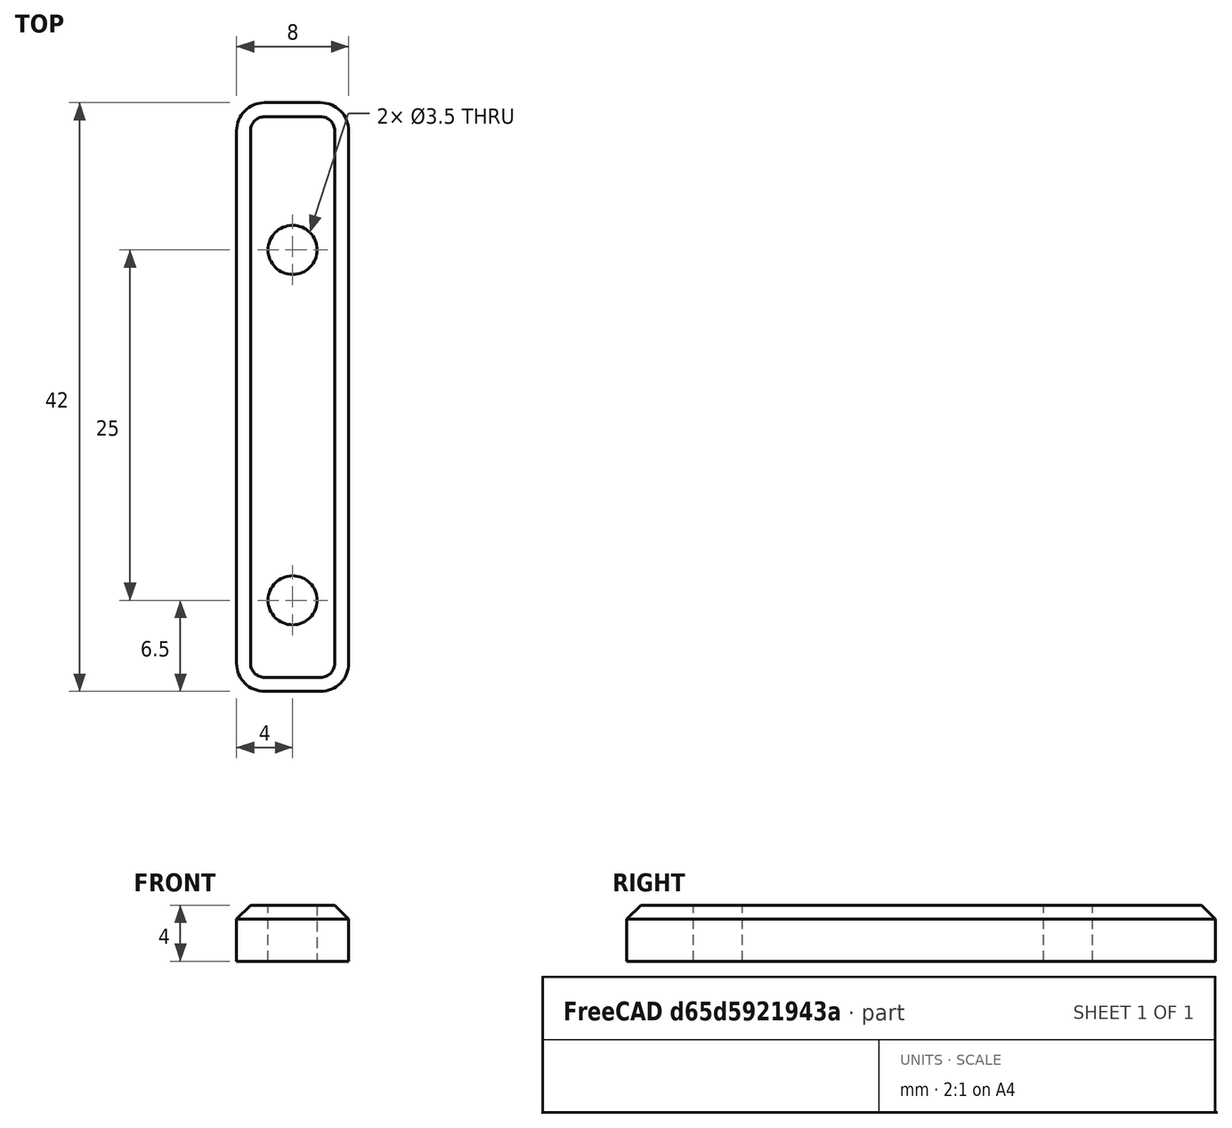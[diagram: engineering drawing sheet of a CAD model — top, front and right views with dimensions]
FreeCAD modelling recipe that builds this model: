
FCSTD DOCUMENT  (FreeCAD 0.19R)
Label: HeadClamp2
License: All rights reserved
LicenseURL: http://en.wikipedia.org/wiki/All_rights_reserved
objects: Sketcher::SketchObject×2, PartDesign::Pad×1, PartDesign::Pocket×1, PartDesign::Fillet×1, PartDesign::Chamfer×1, PartDesign::Body×1, Mesh::Feature×1
note: 11 computed .brp shape members not serialized (recipe doc carries the construction recipe); baked Part::Feature solids carry a one-line shape summary decoded from their .brp

FEATURE [Sketcher::SketchObject] Sketch
  FullyConstrained = true
  MapMode = 5
  Support = -> [XY_Plane]
  sketch-geometry (4):
    g0: LineSegment StartX=-4 StartY=50 StartZ=0 EndX=4 EndY=50 EndZ=0
    g1: LineSegment StartX=4 StartY=50 StartZ=0 EndX=4 EndY=8 EndZ=0
    g2: LineSegment StartX=4 StartY=8 StartZ=0 EndX=-4 EndY=8 EndZ=0
    g3: LineSegment StartX=-4 StartY=8 StartZ=0 EndX=-4 EndY=50 EndZ=0
  constraints (11):
    c: Coincident(g0,g1)
    c: Coincident(g1,g2)
    c: Coincident(g2,g3)
    c: Coincident(g3,g0)
    c: Horizontal(g2)
    c: Vertical(g1)
    c: Vertical(g3)
    c: Distance(g0) = 8
    c: Symmetric(g0,g0,g-2)
    c: DistanceY(g0) = 50
    c: DistanceY(g1) = 8
FEATURE [PartDesign::Pad] Pad
  Direction = (1,1,1)
  Length = 4
  Length2 = 100
  Profile = -> Sketch
  Type = 0
FEATURE [Sketcher::SketchObject] Sketch001
  FullyConstrained = true
  MapMode = 5
  Placement = pos=(0,0,4) rot=(0,0,1;0rad)
  Support = -> [Pad]
  sketch-geometry (2):
    g0: Circle CenterX=0 CenterY=14.5 CenterZ=0 NormalX=0 NormalY=0 NormalZ=1 AngleXU=0 Radius=1.75
    g1: Circle CenterX=0 CenterY=39.5 CenterZ=0 NormalX=0 NormalY=0 NormalZ=1 AngleXU=0 Radius=1.75
  constraints (6):
    c: Diameter(g1) = 3.5
    c: Equal(g1,g0)
    c: PointOnObject(g1,g-2)
    c: PointOnObject(g0,g-2)
    c: DistanceY(g0) = 14.5
    c: DistanceY(g1) = 39.5
FEATURE [PartDesign::Pocket] Pocket
  BaseFeature = -> Pad
  Length = 5
  Length2 = 100
  Profile = -> Sketch001
  Type = 0
FEATURE [PartDesign::Fillet] Fillet
  Base = -> Pocket [Edge2,Edge1,Edge8,Edge5]
  BaseFeature = -> Pocket
  Radius = 2
  SupportTransform = false
FEATURE [PartDesign::Chamfer] Chamfer
  Angle = 45
  Base = -> Fillet [Edge19]
  BaseFeature = -> Fillet
  ChamferType = 0
  FlipDirection = false
  Size = 1
  Size2 = 1
  SupportTransform = false
FEATURE [PartDesign::Body] Body
  Group = -> [Sketch,Pad,Sketch001,Pocket,Fillet,Chamfer]
  Origin = -> Origin
  Tip = -> Chamfer
FEATURE [Mesh::Feature] Mesh  label="Chamfer (Meshed)"
